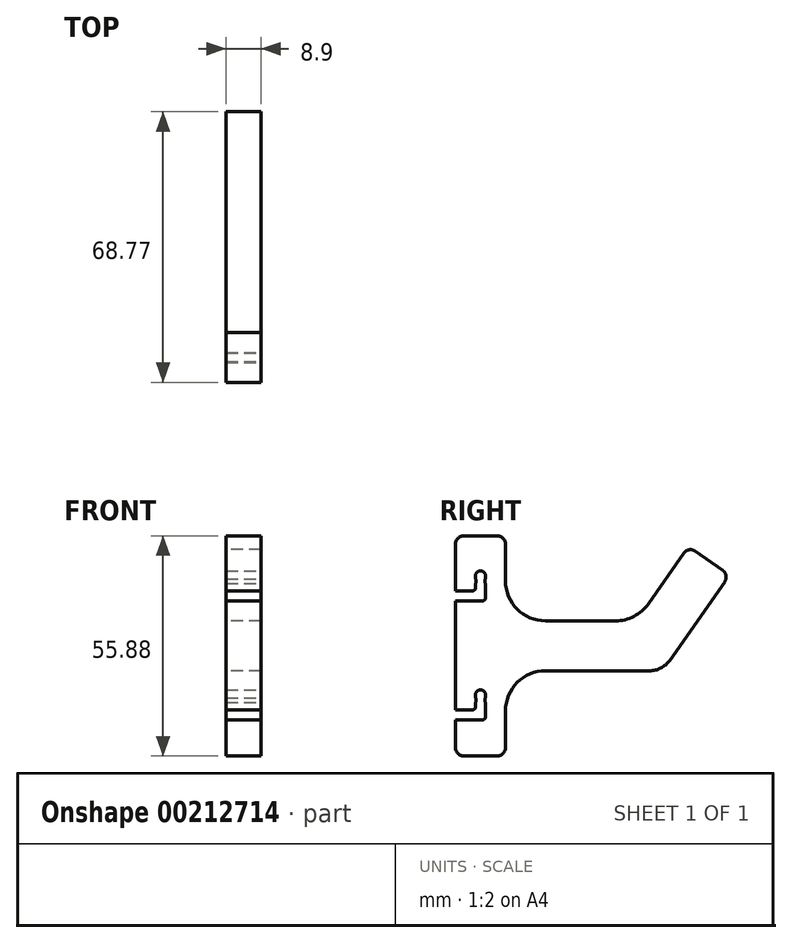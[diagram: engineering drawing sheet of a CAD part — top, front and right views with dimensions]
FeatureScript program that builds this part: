
annotation { "Feature Type Name" : "Feature", "Feature Type Description" : "" }
export const myFeature = defineFeature(function(context is Context, id is Id, definition is map)
    precondition{}
    {
        {
            var Q0;
            Q0=qCreatedBy(makeId("Right.planeOp"),FACE);
            var sketch = newSketch(context, id + "F0", { "sketchPlane" : qUnion([Q0])});
            skLineSegment(sketch, "E0", {"start": v(0, 27.94) * mm, "end": v(12.7, 27.94) * mm});
            skLineSegment(sketch, "E1", {"start": v(12.7, 27.94) * mm, "end": v(12.7, 16.5) * mm});
            skLineSegment(sketch, "E2", {"start": v(0, 0) * mm, "end": v(0, 0) * mm});
            skLineSegment(sketch, "E3", {"start": v(22.86, 6.35) * mm, "end": v(40.64, 6.35) * mm});
            skLineSegment(sketch, "E4", {"start": v(48.96, 10.68) * mm, "end": v(59.16, 25.25) * mm});
            skLineSegment(sketch, "E5", {"start": v(59.16, 25.25) * mm, "end": v(69.56, 17.96) * mm});
            skLineSegment(sketch, "E6", {"start": v(69.56, 17.96) * mm, "end": v(54.44, -3.64) * mm});
            skArc(sketch, "E7", {"start": v(40.64, 6.35) * mm, "mid": v(45.33, 7.5) * mm, "end": v(48.96, 10.68) * mm});
            skArc(sketch, "E8", {"start": v(12.7, 16.5) * mm, "mid": v(15.68, 9.33) * mm, "end": v(22.86, 6.35) * mm});
            skArc(sketch, "E9.filletArc", {"start": v(49.23, -6.35) * mm, "mid": v(52.17, -5.63) * mm, "end": v(54.44, -3.64) * mm});
            skLineSegment(sketch, "E10", {"start": v(22.86, -6.35) * mm, "end": v(49.23, -6.35) * mm});
            skLineSegment(sketch, "E11", {"start": v(0, -27.94) * mm, "end": v(12.7, -27.94) * mm});
            skLineSegment(sketch, "E12", {"start": v(12.7, -27.94) * mm, "end": v(12.7, -16.51) * mm});
            skArc(sketch, "E13.filletArc", {"start": v(22.86, -6.35) * mm, "mid": v(15.68, -9.33) * mm, "end": v(12.7, -16.51) * mm});
            skLineSegment(sketch, "E14", {"start": v(22.86, 6.35) * mm, "end": v(22.86, -6.35) * mm, "construction": true});
            skLineSegment(sketch, "E15", {"start": v(22.86, 0) * mm, "end": v(0, 0) * mm, "construction": true});
            skLineSegment(sketch, "E16", {"start": v(0, 27.94) * mm, "end": v(0, -27.94) * mm});
            skSolve(sketch);
        }
        {
            var Q0;
            Q0=makeQuery(id+"F0.imprint","IMPRINT",FACE,{"disambiguationData":[TD([[makeQuery(id+"F0.imprint","IMPRINT",EDGE,{"derivedFrom":sQuery(id+"F0.wireOp",EDGE,"R0l6xUIm-IaAg-fqYT-cFUw-Lf6RCEfInmms")}),-1.0]])]});
            var Q1;
            Q1=makeQuery(id+"F0.imprint","IMPRINT",FACE,{"disambiguationData":[TD([[makeQuery(id+"F0.imprint","IMPRINT",EDGE,{"derivedFrom":sQuery(id+"F0.wireOp",EDGE,"E0")}),-1.0]])]});
            extrude(context, id + "F1", {"entities" : qUnion([Q0, Q1]), "offsetDistance" : 25 * mm, "depth" : 8.9 * mm, "symmetric" : true});
        }
        {
            var Q0;
            Q0=makeQuery(id+"F1.opExtrude","SWEPT_EDGE",EDGE,{"disambiguationData":[OSD([sQuery(id+"F0.wireOp",EDGE,"E0"),sQuery(id+"F0.wireOp",EDGE,"E1")])]});
            var Q1;
            Q1=makeQuery(id+"F1.opExtrude","SWEPT_EDGE",EDGE,{"disambiguationData":[OSD([sQuery(id+"F0.wireOp",EDGE,"do6iOSd0-p59h-Iph2-EZYE-FqhHj6ALnol1"),sQuery(id+"F0.wireOp",EDGE,"T0NzOJQf-1ohU-N6pa-0O5Z-Gt8aX7xeZM4e")])]});
            var Q2;
            Q2=makeQuery(id+"F1.opExtrude","SWEPT_EDGE",EDGE,{"disambiguationData":[OSD([sQuery(id+"F0.wireOp",EDGE,"do6iOSd0-p59h-Iph2-EZYE-FqhHj6ALnol1"),sQuery(id+"F0.wireOp",EDGE,"WKioYHe8-msfK-nLwt-kgpN-sC7kTCiPyutY")])]});
            var Q3;
            Q3=makeQuery(id+"F1.opExtrude","SWEPT_EDGE",EDGE,{"disambiguationData":[OSD([sQuery(id+"F0.wireOp",EDGE,"do6iOSd0-p59h-Iph2-EZYE-FqhHj6ALnol1"),sQuery(id+"F0.wireOp",EDGE,"T0NzOJQf-1ohU-N6pa-0O5Z-Gt8aX7xeZM4e")])]});
            var Q4;
            Q4=makeQuery(id+"F1.opExtrude","SWEPT_EDGE",EDGE,{"disambiguationData":[OSD([sQuery(id+"F0.wireOp",EDGE,"do6iOSd0-p59h-Iph2-EZYE-FqhHj6ALnol1"),sQuery(id+"F0.wireOp",EDGE,"WKioYHe8-msfK-nLwt-kgpN-sC7kTCiPyutY")])]});
            var Q5;
            Q5=makeQuery(id+"F1.opExtrude","SWEPT_EDGE",EDGE,{"disambiguationData":[OSD([sQuery(id+"F0.wireOp",EDGE,"E0"),sQuery(id+"F0.wireOp",EDGE,"917d6a71-8020-47b3-91d0-356564592358.trimOffspring")])]});
            var Q6;
            Q6=makeQuery(id+"F1.opExtrude","SWEPT_EDGE",EDGE,{"disambiguationData":[OSD([sQuery(id+"F0.wireOp",EDGE,"E0"),sQuery(id+"F0.wireOp",EDGE,"E1")])]});
            var Q7;
            Q7=makeQuery(id+"F1.opExtrude","SWEPT_EDGE",EDGE,{"disambiguationData":[OSD([sQuery(id+"F0.wireOp",EDGE,"E0"),sQuery(id+"F0.wireOp",EDGE,"917d6a71-8020-47b3-91d0-356564592358.trimOffspring")])]});
            var Q8;
            Q8=makeQuery(id+"F1.opExtrude","SWEPT_EDGE",EDGE,{"disambiguationData":[OSD([sQuery(id+"F0.wireOp",EDGE,"E0"),sQuery(id+"F0.wireOp",EDGE,"917d6a71-8020-47b3-91d0-356564592358.trimOffspring")])]});
            var Q9;
            Q9=makeQuery(id+"F1.opExtrude","SWEPT_EDGE",EDGE,{"disambiguationData":[OSD([sQuery(id+"F0.wireOp",EDGE,"917d6a71-8020-47b3-91d0-356564592358.trimOffspring"),sQuery(id+"F0.wireOp",EDGE,"oMnLxIvI-c7EB-dOBx-Ktot-nHqWXF2Je9gS")])]});
            var Q10;
            Q10=makeQuery(id+"F1.opExtrude","SWEPT_EDGE",EDGE,{"disambiguationData":[OSD([sQuery(id+"F0.wireOp",EDGE,"R0l6xUIm-IaAg-fqYT-cFUw-Lf6RCEfInmms"),sQuery(id+"F0.wireOp",EDGE,"H5s6PmsO-nB2p-iTXC-beMi-EFhrGGPzX9zd")])]});
            var Q11;
            Q11=makeQuery(id+"F1.opExtrude","SWEPT_EDGE",EDGE,{"disambiguationData":[OSD([sQuery(id+"F0.wireOp",EDGE,"R0l6xUIm-IaAg-fqYT-cFUw-Lf6RCEfInmms"),sQuery(id+"F0.wireOp",EDGE,"H5s6PmsO-nB2p-iTXC-beMi-EFhrGGPzX9zd")])]});
            var Q12;
            Q12=makeQuery(id+"F1.opExtrude","SWEPT_EDGE",EDGE,{"disambiguationData":[OSD([sQuery(id+"F0.wireOp",EDGE,"R0l6xUIm-IaAg-fqYT-cFUw-Lf6RCEfInmms"),sQuery(id+"F0.wireOp",EDGE,"H5s6PmsO-nB2p-iTXC-beMi-EFhrGGPzX9zd")])]});
            var Q13;
            Q13=makeQuery(id+"F1.opExtrude","SWEPT_EDGE",EDGE,{"disambiguationData":[OSD([sQuery(id+"F0.wireOp",EDGE,"R0l6xUIm-IaAg-fqYT-cFUw-Lf6RCEfInmms"),sQuery(id+"F0.wireOp",EDGE,"H5s6PmsO-nB2p-iTXC-beMi-EFhrGGPzX9zd")])]});
            var Q14;
            Q14=makeQuery(id+"F1.opExtrude","SWEPT_EDGE",EDGE,{"disambiguationData":[OSD([sQuery(id+"F0.wireOp",EDGE,"tsVY66jG-GQxW-Nj7m-msUx-ij5FFVlZpnMZ"),sQuery(id+"F0.wireOp",EDGE,"p4fpiYAK-jGJt-w9eP-5vz1-EoqmOrb9To5q")])]});
            var Q15;
            Q15=makeQuery(id+"F1.opExtrude","SWEPT_EDGE",EDGE,{"disambiguationData":[OSD([sQuery(id+"F0.wireOp",EDGE,"tsVY66jG-GQxW-Nj7m-msUx-ij5FFVlZpnMZ"),sQuery(id+"F0.wireOp",EDGE,"pGC2duow-bWWV-YhgJ-DpL9-4p7fWgwL10ZT")])]});
            var Q16;
            Q16=makeQuery(id+"F1.opExtrude","SWEPT_EDGE",EDGE,{"disambiguationData":[OSD([sQuery(id+"F0.wireOp",EDGE,"tsVY66jG-GQxW-Nj7m-msUx-ij5FFVlZpnMZ"),sQuery(id+"F0.wireOp",EDGE,"pGC2duow-bWWV-YhgJ-DpL9-4p7fWgwL10ZT")])]});
            var Q17;
            Q17=makeQuery(id+"F1.opExtrude","SWEPT_EDGE",EDGE,{"disambiguationData":[OSD([sQuery(id+"F0.wireOp",EDGE,"tsVY66jG-GQxW-Nj7m-msUx-ij5FFVlZpnMZ"),sQuery(id+"F0.wireOp",EDGE,"p4fpiYAK-jGJt-w9eP-5vz1-EoqmOrb9To5q")])]});
            var Q18;
            Q18=makeQuery(id+"F1.opExtrude","SWEPT_EDGE",EDGE,{"disambiguationData":[OSD([sQuery(id+"F0.wireOp",EDGE,"tsVY66jG-GQxW-Nj7m-msUx-ij5FFVlZpnMZ"),sQuery(id+"F0.wireOp",EDGE,"pGC2duow-bWWV-YhgJ-DpL9-4p7fWgwL10ZT")])]});
            var Q19;
            Q19=makeQuery(id+"F1.opExtrude","SWEPT_EDGE",EDGE,{"disambiguationData":[OSD([sQuery(id+"F0.wireOp",EDGE,"l7jfHRW3-1uXe-nOm0-suk0-xWNmDAWcYurH"),sQuery(id+"F0.wireOp",EDGE,"E2")])]});
            var Q20;
            Q20=makeQuery(id+"F1.opExtrude","SWEPT_EDGE",EDGE,{"disambiguationData":[OSD([sQuery(id+"F0.wireOp",EDGE,"E4"),sQuery(id+"F0.wireOp",EDGE,"E5")])]});
            var Q21;
            Q21=makeQuery(id+"F1.opExtrude","SWEPT_EDGE",EDGE,{"disambiguationData":[OSD([sQuery(id+"F0.wireOp",EDGE,"E5"),sQuery(id+"F0.wireOp",EDGE,"E6")])]});
            var Q22;
            Q22=makeQuery(id+"F1.opExtrude","SWEPT_EDGE",EDGE,{"disambiguationData":[OSD([sQuery(id+"F0.wireOp",EDGE,"HwGaTEn9-BNxz-0WnA-syz4-q6Jnh5qYwC56"),sQuery(id+"F0.wireOp",EDGE,"E10")])]});
            var Q23;
            Q23=makeQuery(id+"F1.opExtrude","SWEPT_EDGE",EDGE,{"disambiguationData":[OSD([sQuery(id+"F0.wireOp",EDGE,"E11"),sQuery(id+"F0.wireOp",EDGE,"E12")])]});
            var Q24;
            Q24=makeQuery(id+"F1.opExtrude","SWEPT_EDGE",EDGE,{"disambiguationData":[OSD([sQuery(id+"F0.wireOp",EDGE,"E11"),sQuery(id+"F0.wireOp",EDGE,"E16")])]});
            fillet(context, id + "F2", {"entities" : qUnion([Q0, Q1, Q2, Q3, Q4, Q5, Q6, Q7, Q8, Q9, Q10, Q11, Q12, Q13, Q14, Q15, Q16, Q17, Q18, Q19, Q20, Q21, Q22, Q23, Q24]), "radius" : 2.03 * mm, "tangentPropagation" : true, "defaultsChanged" : false, "vertexSettings" : [], "allowEdgeOverflow" : false});
        }
        {
            var Q0;
            Q0=makeQuery(id+"F1.opExtrude","CAP_FACE",FACE,{"disambiguationData":[OSD([sQuery(id+"F0.wireOp",EDGE,"R0l6xUIm-IaAg-fqYT-cFUw-Lf6RCEfInmms"),sQuery(id+"F0.wireOp",EDGE,"E0"),sQuery(id+"F0.wireOp",EDGE,"917d6a71-8020-47b3-91d0-356564592358.trimOffspring"),sQuery(id+"F0.wireOp",EDGE,"do6iOSd0-p59h-Iph2-EZYE-FqhHj6ALnol1"),sQuery(id+"F0.wireOp",EDGE,"E1"),sQuery(id+"F0.wireOp",EDGE,"oMnLxIvI-c7EB-dOBx-Ktot-nHqWXF2Je9gS"),sQuery(id+"F0.wireOp",EDGE,"H5s6PmsO-nB2p-iTXC-beMi-EFhrGGPzX9zd"),sQuery(id+"F0.wireOp",EDGE,"E55nDa4c-AnYE-asiw-xueP-FGOoVfwC6I5W"),sQuery(id+"F0.wireOp",EDGE,"tsVY66jG-GQxW-Nj7m-msUx-ij5FFVlZpnMZ"),sQuery(id+"F0.wireOp",EDGE,"WKioYHe8-msfK-nLwt-kgpN-sC7kTCiPyutY"),sQuery(id+"F0.wireOp",EDGE,"pGC2duow-bWWV-YhgJ-DpL9-4p7fWgwL10ZT"),sQuery(id+"F0.wireOp",EDGE,"l7jfHRW3-1uXe-nOm0-suk0-xWNmDAWcYurH"),sQuery(id+"F0.wireOp",EDGE,"p4fpiYAK-jGJt-w9eP-5vz1-EoqmOrb9To5q"),sQuery(id+"F0.wireOp",EDGE,"E2"),sQuery(id+"F0.wireOp",EDGE,"yA7TRvCN-UMRo-vrpZ-Ydxq-uWrTOSylFOQI"),sQuery(id+"F0.wireOp",EDGE,"T0NzOJQf-1ohU-N6pa-0O5Z-Gt8aX7xeZM4e"),sQuery(id+"F0.wireOp",EDGE,"pUJUahGI-wT5O-X5Pp-sLFv-ISeCsSa39cJM"),sQuery(id+"F0.wireOp",EDGE,"gnTElwEQ-xExs-yJdp-y54U-xUUldCR7EacK"),sQuery(id+"F0.wireOp",EDGE,"427NVwON-J4Eg-A1F7-4Q2u-34sglIcidLrh")])],"isStart":false});
            var sketch = newSketch(context, id + "F3", { "sketchPlane" : qUnion([Q0])});
            skLineSegment(sketch, "E17", {"start": v(6.35, 17.78) * mm, "end": v(6.35, -12.45) * mm, "construction": true});
            skArc(sketch, "E18", {"start": v(7.62, 17.78) * mm, "mid": v(6.35, 19.05) * mm, "end": v(5.08, 17.78) * mm});
            skLineSegment(sketch, "E19", {"start": v(5.08, 17.78) * mm, "end": v(5.08, 13.97) * mm});
            skLineSegment(sketch, "E20", {"start": v(7.62, 11.43) * mm, "end": v(0, 11.43) * mm});
            skLineSegment(sketch, "E21", {"start": v(7.62, 11.43) * mm, "end": v(7.62, 17.78) * mm});
            skLineSegment(sketch, "E22", {"start": v(6.35, 17.78) * mm, "end": v(6.35, 27.94) * mm, "construction": true});
            skArc(sketch, "E23", {"start": v(7.62, -12.45) * mm, "mid": v(6.35, -11.18) * mm, "end": v(5.08, -12.45) * mm});
            skLineSegment(sketch, "E24", {"start": v(5.08, -12.45) * mm, "end": v(5.08, -16.26) * mm});
            skLineSegment(sketch, "E25", {"start": v(5.08, -16.26) * mm, "end": v(0, -16.26) * mm});
            skLineSegment(sketch, "E26", {"start": v(0, -16.26) * mm, "end": v(0, -18.8) * mm});
            skLineSegment(sketch, "E27", {"start": v(0, -18.8) * mm, "end": v(7.62, -18.8) * mm});
            skLineSegment(sketch, "E28", {"start": v(7.62, -18.8) * mm, "end": v(7.62, -12.45) * mm});
            skLineSegment(sketch, "E29", {"start": v(5.08, 13.97) * mm, "end": v(0, 13.97) * mm});
            skLineSegment(sketch, "E30", {"start": v(0, 13.97) * mm, "end": v(0, 11.43) * mm});
            skSolve(sketch);
        }
        {
            var Q0;
            Q0=qSketchRegion(id+"F3",true);
            extrude(context, id + "F4", {"entities" : qUnion([Q0]), "operationType" : NewBodyOperationType.REMOVE, "endBound" : BoundingType.THROUGH_ALL, "oppositeDirection" : true, "depth" : 25.4 * mm});
        }
        {
            var Q0;
            Q0=makeQuery(id+"F4.boolean.opBoolean","COPY",EDGE,{"derivedFrom":makeQuery(id+"F4.opExtrude","SWEPT_EDGE",EDGE,{"disambiguationData":[OSD([sQuery(id+"F3.wireOp",EDGE,"E20"),sQuery(id+"F3.wireOp",EDGE,"E21")])]})});
            var Q1;
            Q1=makeQuery(id+"F4.boolean.opBoolean","COPY",EDGE,{"derivedFrom":makeQuery(id+"F4.opExtrude","SWEPT_EDGE",EDGE,{"disambiguationData":[OSD([sQuery(id+"F0.wireOp",EDGE,"E1"),sQuery(id+"F3.wireOp",EDGE,"ZqR5sxNf-ryuF-6MKE-6XIY-ClZdcAyAqOEV"),sQuery(id+"F3.wireOp",EDGE,"E20")])]})});
            var Q2;
            Q2=makeQuery(id+"F4.boolean.opBoolean","COPY",EDGE,{"derivedFrom":makeQuery(id+"F4.opExtrude","SWEPT_EDGE",EDGE,{"disambiguationData":[OSD([sQuery(id+"F3.wireOp",EDGE,"E19"),sQuery(id+"F3.wireOp",EDGE,"8UhXKb6Y-CDqS-eFG7-f0vi-MXKg6AltH5Fs")])]})});
            var Q3;
            Q3=makeQuery(id+"F4.boolean.opBoolean","COPY",EDGE,{"derivedFrom":makeQuery(id+"F4.opExtrude","SWEPT_EDGE",EDGE,{"disambiguationData":[OSD([sQuery(id+"F0.wireOp",EDGE,"E1"),sQuery(id+"F3.wireOp",EDGE,"8UhXKb6Y-CDqS-eFG7-f0vi-MXKg6AltH5Fs"),sQuery(id+"F3.wireOp",EDGE,"ZqR5sxNf-ryuF-6MKE-6XIY-ClZdcAyAqOEV")])]})});
            var Q4;
            Q4=makeQuery(id+"F4.boolean.opBoolean","COPY",EDGE,{"derivedFrom":makeQuery(id+"F4.opExtrude","SWEPT_EDGE",EDGE,{"disambiguationData":[OSD([sQuery(id+"F0.wireOp",EDGE,"R0l6xUIm-IaAg-fqYT-cFUw-Lf6RCEfInmms"),sQuery(id+"F0.wireOp",EDGE,"E2"),sQuery(id+"F3.wireOp",EDGE,"E25"),sQuery(id+"F3.wireOp",EDGE,"E26")])]})});
            var Q5;
            Q5=makeQuery(id+"F4.boolean.opBoolean","COPY",EDGE,{"derivedFrom":makeQuery(id+"F4.opExtrude","SWEPT_EDGE",EDGE,{"disambiguationData":[OSD([sQuery(id+"F3.wireOp",EDGE,"E27"),sQuery(id+"F3.wireOp",EDGE,"E28")])]})});
            var Q6;
            Q6=makeQuery(id+"F4.boolean.opBoolean","COPY",EDGE,{"derivedFrom":makeQuery(id+"F4.opExtrude","SWEPT_EDGE",EDGE,{"disambiguationData":[OSD([sQuery(id+"F0.wireOp",EDGE,"R0l6xUIm-IaAg-fqYT-cFUw-Lf6RCEfInmms"),sQuery(id+"F0.wireOp",EDGE,"E2"),sQuery(id+"F3.wireOp",EDGE,"E26"),sQuery(id+"F3.wireOp",EDGE,"E27")])]})});
            var Q7;
            Q7=makeQuery(id+"F4.boolean.opBoolean","COPY",EDGE,{"derivedFrom":makeQuery(id+"F4.opExtrude","SWEPT_EDGE",EDGE,{"disambiguationData":[OSD([sQuery(id+"F3.wireOp",EDGE,"E24"),sQuery(id+"F3.wireOp",EDGE,"E25")])]})});
            fillet(context, id + "F5", {"entities" : qUnion([Q0, Q1, Q2, Q3, Q4, Q5, Q6, Q7]), "radius" : 0.76 * mm, "tangentPropagation" : true, "allowEdgeOverflow" : false});
        }
        {
            var Q0;
            Q0=makeQuery(id+"F1.opExtrude","CAP_FACE",FACE,{"disambiguationData":[OSD([sQuery(id+"F0.wireOp",EDGE,"R0l6xUIm-IaAg-fqYT-cFUw-Lf6RCEfInmms"),sQuery(id+"F0.wireOp",EDGE,"E0"),sQuery(id+"F0.wireOp",EDGE,"E1"),sQuery(id+"F0.wireOp",EDGE,"tsVY66jG-GQxW-Nj7m-msUx-ij5FFVlZpnMZ"),sQuery(id+"F0.wireOp",EDGE,"WKioYHe8-msfK-nLwt-kgpN-sC7kTCiPyutY"),sQuery(id+"F0.wireOp",EDGE,"pGC2duow-bWWV-YhgJ-DpL9-4p7fWgwL10ZT"),sQuery(id+"F0.wireOp",EDGE,"l7jfHRW3-1uXe-nOm0-suk0-xWNmDAWcYurH"),sQuery(id+"F0.wireOp",EDGE,"p4fpiYAK-jGJt-w9eP-5vz1-EoqmOrb9To5q"),sQuery(id+"F0.wireOp",EDGE,"E2")])],"isStart":false});
            var sketch = newSketch(context, id + "F6", { "sketchPlane" : qUnion([Q0])});
            skArc(sketch, "E31", {"start": v(5.08, 15.85) * mm, "mid": v(5.25, 16.45) * mm, "end": v(5.08, 17.05) * mm});
            skLineSegment(sketch, "E32", {"start": v(5.08, 15.85) * mm, "end": v(7.62, 15.85) * mm, "construction": true});
            skLineSegment(sketch, "E33", {"start": v(5.08, 17.05) * mm, "end": v(7.62, 17.05) * mm, "construction": true});
            skLineSegment(sketch, "E34", {"start": v(5.08, 17.05) * mm, "end": v(5.08, 15.85) * mm});
            skLineSegment(sketch, "E35", {"start": v(6.35, 17.78) * mm, "end": v(6.35, -12.45) * mm, "construction": true});
            skArc(sketch, "E36", {"start": v(7.62, 17.05) * mm, "mid": v(7.45, 16.45) * mm, "end": v(7.62, 15.85) * mm});
            skLineSegment(sketch, "E37", {"start": v(7.62, 17.05) * mm, "end": v(7.62, 15.85) * mm});
            skArc(sketch, "E38.1.0.0", {"start": v(5.08, -14.37) * mm, "mid": v(5.25, -13.78) * mm, "end": v(5.08, -13.18) * mm});
            skLineSegment(sketch, "E38.1.0.1", {"start": v(5.08, -13.18) * mm, "end": v(5.08, -14.37) * mm});
            skArc(sketch, "E38.1.0.2", {"start": v(7.62, -13.18) * mm, "mid": v(7.45, -13.78) * mm, "end": v(7.62, -14.37) * mm});
            skLineSegment(sketch, "E38.1.0.3", {"start": v(7.62, -13.18) * mm, "end": v(7.62, -14.37) * mm});
            skLineSegment(sketch, "E38.direction1", {"start": v(4.1, 16.45) * mm, "end": v(4.1, -13.78) * mm, "construction": true});
            skSolve(sketch);
        }
        {
            var Q0;
            Q0=makeQuery(id+"F6.imprint","IMPRINT",FACE,{"disambiguationData":[TD([[makeQuery(id+"F6.imprint","IMPRINT",EDGE,{"derivedFrom":sQuery(id+"F6.wireOp",EDGE,"d457577a-73cc-4f87-a162-efa161ee7ef10.MirrorCS")}),-1.0]])]});
            var Q1;
            Q1=makeQuery(id+"F6.imprint","IMPRINT",FACE,{"disambiguationData":[TD([[makeQuery(id+"F6.imprint","IMPRINT",EDGE,{"derivedFrom":sQuery(id+"F6.wireOp",EDGE,"E31")}),1.0]])]});
            var Q2;
            Q2=makeQuery(id+"F6.imprint","IMPRINT",FACE,{"disambiguationData":[TD([[makeQuery(id+"F6.imprint","IMPRINT",EDGE,{"derivedFrom":sQuery(id+"F6.wireOp",EDGE,"3d5582df-7b79-4c8f-a72e-c11ca9ff15ec0.MirrorCS")}),1.0]])]});
            var Q3;
            Q3=makeQuery(id+"F6.imprint","IMPRINT",FACE,{"disambiguationData":[TD([[makeQuery(id+"F6.imprint","IMPRINT",EDGE,{"derivedFrom":sQuery(id+"F6.wireOp",EDGE,"959f3de2-425d-4b12-b61e-e030c7eec4390.MirrorCS")}),1.0]])]});
            var Q4;
            Q4=makeQuery(id+"F6.imprint","IMPRINT",FACE,{"disambiguationData":[TD([[makeQuery(id+"F6.imprint","IMPRINT",EDGE,{"derivedFrom":sQuery(id+"F6.wireOp",EDGE,"E38.1.0.0")}),1.0]])]});
            var Q5;
            Q5=makeQuery(id+"F6.imprint","IMPRINT",FACE,{"disambiguationData":[TD([[makeQuery(id+"F6.imprint","IMPRINT",EDGE,{"derivedFrom":sQuery(id+"F6.wireOp",EDGE,"E38.1.0.2")}),1.0]])]});
            var Q6;
            Q6=makeQuery(id+"F6.imprint","IMPRINT",FACE,{"disambiguationData":[TD([[makeQuery(id+"F6.imprint","IMPRINT",EDGE,{"derivedFrom":sQuery(id+"F6.wireOp",EDGE,"E36")}),1.0]])]});
            var Q7;
            Q7=makeQuery(id+"F1.opExtrude","CAP_FACE",FACE,{"disambiguationData":[OSD([sQuery(id+"F0.wireOp",EDGE,"R0l6xUIm-IaAg-fqYT-cFUw-Lf6RCEfInmms"),sQuery(id+"F0.wireOp",EDGE,"E0"),sQuery(id+"F0.wireOp",EDGE,"E1"),sQuery(id+"F0.wireOp",EDGE,"tsVY66jG-GQxW-Nj7m-msUx-ij5FFVlZpnMZ"),sQuery(id+"F0.wireOp",EDGE,"WKioYHe8-msfK-nLwt-kgpN-sC7kTCiPyutY"),sQuery(id+"F0.wireOp",EDGE,"pGC2duow-bWWV-YhgJ-DpL9-4p7fWgwL10ZT"),sQuery(id+"F0.wireOp",EDGE,"l7jfHRW3-1uXe-nOm0-suk0-xWNmDAWcYurH"),sQuery(id+"F0.wireOp",EDGE,"p4fpiYAK-jGJt-w9eP-5vz1-EoqmOrb9To5q"),sQuery(id+"F0.wireOp",EDGE,"E2")])],"isStart":true});
            extrude(context, id + "F7", {"entities" : qUnion([Q0, Q1, Q2, Q3, Q4, Q5, Q6]), "operationType" : NewBodyOperationType.ADD, "endBound" : BoundingType.UP_TO_SURFACE, "oppositeDirection" : true, "endBoundEntityFace" : qUnion([Q7]), "offsetDistance" : 25 * mm, "depth" : 25.4 * mm});
        }
    });
